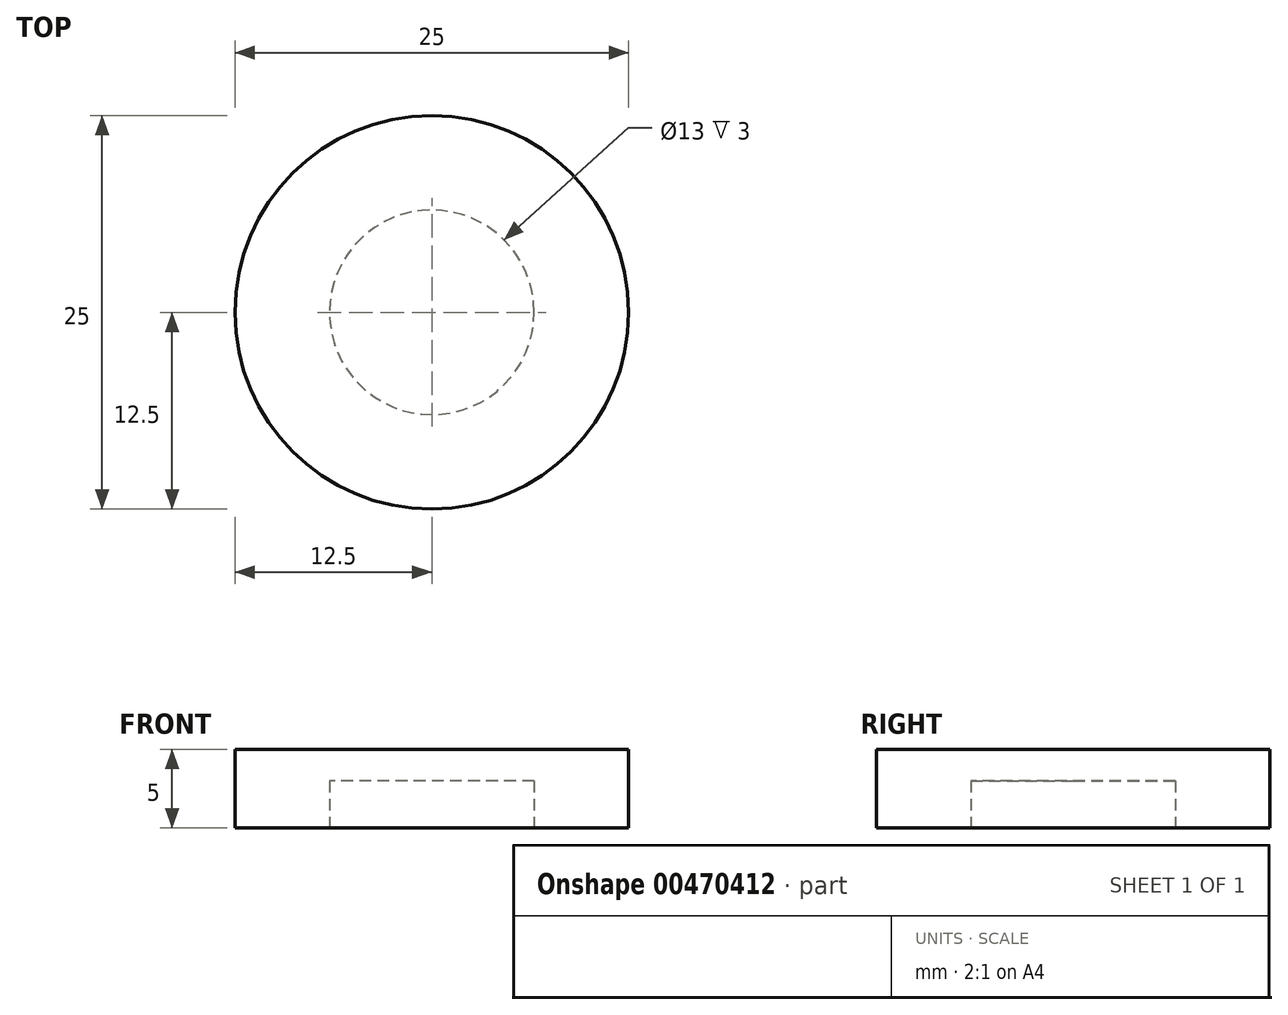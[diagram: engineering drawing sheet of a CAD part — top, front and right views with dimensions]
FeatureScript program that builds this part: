
annotation { "Feature Type Name" : "Feature", "Feature Type Description" : "" }
export const myFeature = defineFeature(function(context is Context, id is Id, definition is map)
    precondition{}
    {
        {
            var Q0;
            Q0=qCreatedBy(makeId("Top.planeOp"),FACE);
            var sketch = newSketch(context, id + "F0", { "sketchPlane" : qUnion([Q0])});
            skCircle(sketch, "E0", {"center": v(0, 0) * mm, "radius": 12.5 * mm});
            skSolve(sketch);
        }
        {
            var Q0;
            Q0=makeQuery(id+"F0.imprint","IMPRINT",FACE,{"disambiguationData":[TD([[makeQuery(id+"F0.imprint","IMPRINT",EDGE,{"derivedFrom":sQuery(id+"F0.wireOp",EDGE,"E0")}),1.0]])]});
            extrude(context, id + "F1", {"entities" : qUnion([Q0]), "depth" : 5 * mm});
        }
        {
            var Q0;
            Q0=qCreatedBy(makeId("Top.planeOp"),FACE);
            var sketch = newSketch(context, id + "F2", { "sketchPlane" : qUnion([Q0])});
            skCircle(sketch, "E1", {"center": v(0, 0) * mm, "radius": 6.5 * mm});
            skSolve(sketch);
        }
        {
            var Q0;
            Q0=makeQuery(id+"F2.imprint","IMPRINT",FACE,{"disambiguationData":[TD([[makeQuery(id+"F2.imprint","IMPRINT",EDGE,{"derivedFrom":sQuery(id+"F2.wireOp",EDGE,"E1")}),1.0]])]});
            extrude(context, id + "F3", {"entities" : qUnion([Q0]), "operationType" : NewBodyOperationType.ADD, "depth" : 2.54 * mm});
        }
        {
            var Q0;
            Q0 = qSketchRegion(id + "F2", true);
            extrude(context, id + "F4", {"entities" : qUnion([Q0]), "operationType" : NewBodyOperationType.ADD, "depth" : 3 * mm});
        }
        {
            var Q0;
            Q0=qCreatedBy(makeId("Top.planeOp"),FACE);
            var sketch = newSketch(context, id + "F5", { "sketchPlane" : qUnion([Q0])});
            skCircle(sketch, "E2", {"center": v(0, 0) * mm, "radius": 6.5 * mm});
            skSolve(sketch);
        }
        {
            var Q0;
            Q0=makeQuery(id+"F5.imprint","IMPRINT",FACE,{"disambiguationData":[TD([[makeQuery(id+"F5.imprint","IMPRINT",EDGE,{"derivedFrom":sQuery(id+"F5.wireOp",EDGE,"E2")}),1.0]])]});
            extrude(context, id + "F6", {"entities" : qUnion([Q0]), "operationType" : NewBodyOperationType.REMOVE, "oppositeDirection" : true, "depth" : -3 * mm});
        }
    });
